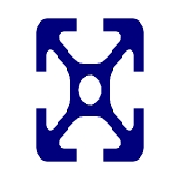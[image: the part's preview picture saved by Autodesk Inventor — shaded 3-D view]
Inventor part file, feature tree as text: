
AUTODESK INVENTOR PART (.ipt)
format: ipt  version: 2020 (Build 240168000, 168)  size: 273,408 bytes
history: native  units: mm
features: other x16, sketch x8
ambient origin geometry x8: Origin, YZ Plane, XZ Plane, XY Plane, X Axis, Y Axis, Z Axis, Center Point
bodies: Body (feature_tree)
feature tree (24):
  other  "Řízená délka"
  other  "Těleso1"
  other  "Start Plane"
  other  "End Plane"
  other  "iFeatureSketch"
  other  "DRAZKA_20:1"
  other  "DRAZKA_20:2"
  other  "DRAZKA_20:3"
  other  "DRAZKA_20:4"
  other  "DIRA_20:1"
  other  "DRAZKA_20:1Axis"
  other  "DRAZKA_20:2Axis"
  other  "DRAZKA_20:3Axis"
  other  "DRAZKA_20:4Axis"
  other  "DIRA_20:1Axis"
  sketch  "Sketch"  dims[d2=20.0mm d3=20.0mm d4=2.0mm d9=-0.0mm d10=150.0mm d11=0.13mm d12=0.0mm d15=0.83mm d16=0.83mm d17=9.8mm d18=3.0mm d19=4.55mm d20=45.0deg d21=5.2mm d22=1.8mm d24=1.0mm d26=0.83mm d27=0.83mm d28=9.8mm d29=3.0mm d30=4.55mm d31=45.0deg d32=5.2mm d33=1.8mm d35=1.0mm d37=0.83mm d38=0.83mm d39=9.8mm d40=3.0mm d41=4.55mm d42=45.0deg d43=5.2mm d44=1.8mm d46=1.0mm d48=0.83mm d49=0.83mm d50=9.8mm d51=3.0mm d52=4.55mm d53=45.0deg d54=5.2mm d55=1.8mm d57=1.0mm d59=4.3mm d60=0.0mm d61=0.0mm d62=0.0mm d63=0.0mm d64=0.0mm d65=0.0mm d66=0.0mm d67=0.0mm d76=90.0deg d14=150.0mm]
  sketch  "Náčrt11"
  other  "Pracovní rovina4"
  sketch  "Náčrt12"
  sketch  "Náčrt6"
  sketch  "Náčrt7"
  sketch  "Náčrt8"
  sketch  "Náčrt9"
  sketch  "Náčrt10"
